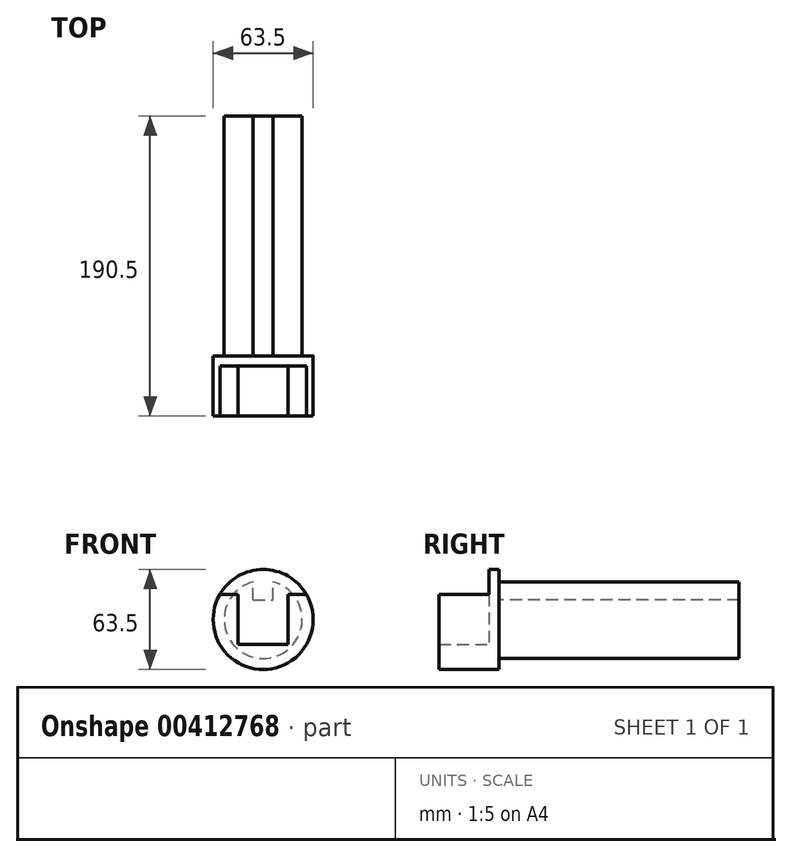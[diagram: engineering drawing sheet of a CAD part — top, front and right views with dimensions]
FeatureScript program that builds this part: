
annotation { "Feature Type Name" : "Feature", "Feature Type Description" : "" }
export const myFeature = defineFeature(function(context is Context, id is Id, definition is map)
    precondition{}
    {
        {
            var Q0;
            Q0=qCreatedBy(makeId("Front.planeOp"),FACE);
            var sketch = newSketch(context, id + "F0", { "sketchPlane" : qUnion([Q0])});
            skArc(sketch, "E0", {"start": v(-27.5, 15.88) * mm, "mid": v(0, -31.75) * mm, "end": v(27.5, 15.88) * mm});
            skLineSegment(sketch, "E1", {"start": v(0, 31.75) * mm, "end": v(0, -31.75) * mm, "construction": true});
            skCircle(sketch, "E2", {"center": v(0, 0) * mm, "radius": 22.45 * mm, "construction": true});
            skLineSegment(sketch, "E3", {"start": v(15.88, 15.88) * mm, "end": v(15.88, -15.88) * mm});
            skLineSegment(sketch, "E4", {"start": v(15.88, -15.88) * mm, "end": v(-15.88, -15.88) * mm});
            skLineSegment(sketch, "E5", {"start": v(-15.88, -15.88) * mm, "end": v(-15.88, 15.88) * mm});
            skLineSegment(sketch, "E6", {"start": v(-15.88, 15.88) * mm, "end": v(-27.5, 15.88) * mm});
            skLineSegment(sketch, "E7", {"start": v(15.88, 15.88) * mm, "end": v(27.5, 15.88) * mm});
            skArc(sketch, "E8", {"start": v(27.5, 15.88) * mm, "mid": v(0, 31.75) * mm, "end": v(-27.5, 15.88) * mm, "construction": true});
            skSolve(sketch);
        }
        {
            var Q0;
            Q0 = qSketchRegion(id + "F0", true);
            extrude(context, id + "F1", {"entities" : qUnion([Q0]), "depth" : 31.75 * mm, "offsetDistance" : 25.4 * mm});
        }
        {
            var Q0;
            Q0=makeQuery(id+"F1.opExtrude","CAP_FACE",FACE,{"disambiguationData":[OSD([sQuery(id+"F0.wireOp",EDGE,"E0"),sQuery(id+"F0.wireOp",EDGE,"ajWhx2Qm-t9gX-1MT6-eZGp-NJe44J70kVmW"),sQuery(id+"F0.wireOp",EDGE,"EVLei9R9-L3Dl-Atgz-0da7-zGIhw3F7YpG8"),sQuery(id+"F0.wireOp",EDGE,"9e28c039-71dc-46a3-9899-5aecf2effe9a0.MirrorCS"),sQuery(id+"F0.wireOp",EDGE,"9e28c039-71dc-46a3-9899-5aecf2effe9a1.MirrorCS")])],"isStart":true});
            var sketch = newSketch(context, id + "F2", { "sketchPlane" : qUnion([Q0])});
            skCircle(sketch, "E9", {"center": v(0, 0) * mm, "radius": 31.75 * mm});
            skSolve(sketch);
        }
        {
            var Q0;
            Q0 = qSketchRegion(id + "F2", true);
            extrude(context, id + "F3", {"entities" : qUnion([Q0]), "operationType" : NewBodyOperationType.ADD, "depth" : 6.35 * mm, "offsetDistance" : 25.4 * mm});
        }
        {
            var Q0;
            Q0=makeQuery(id+"F3.opExtrude","CAP_FACE",FACE,{"disambiguationData":[OSD([sQuery(id+"F2.wireOp",EDGE,"E9")])],"isStart":false});
            var sketch = newSketch(context, id + "F4", { "sketchPlane" : qUnion([Q0])});
            skArc(sketch, "E10.converted", {"start": v(-6.35, 23.94) * mm, "mid": v(0, -24.77) * mm, "end": v(6.35, 23.94) * mm});
            skLineSegment(sketch, "E11", {"start": v(0, 0) * mm, "end": v(0, 24.77) * mm, "construction": true});
            skLineSegment(sketch, "E12", {"start": v(0, 12.38) * mm, "end": v(-6.35, 12.38) * mm});
            skPoint(sketch, "E12.endSnap0", {"position": v(0, 12.38) * mm});
            skLineSegment(sketch, "E13", {"start": v(-6.35, 12.38) * mm, "end": v(-6.35, 23.94) * mm});
            skLineSegment(sketch, "E14.MirrorCS", {"start": v(6.35, 12.38) * mm, "end": v(6.35, 23.94) * mm});
            skLineSegment(sketch, "E15.MirrorCS", {"start": v(0, 12.38) * mm, "end": v(6.35, 12.38) * mm});
            skSolve(sketch);
        }
        {
            var Q0;
            Q0=makeQuery(id+"F4.imprint","IMPRINT",FACE,{"disambiguationData":[TD([[makeQuery(id+"F4.imprint","IMPRINT",EDGE,{"derivedFrom":sQuery(id+"F4.wireOp",EDGE,"E10.converted")}),1.0]])]});
            extrude(context, id + "F5", {"entities" : qUnion([Q0]), "operationType" : NewBodyOperationType.ADD, "depth" : 152.4 * mm, "offsetDistance" : 25.4 * mm});
        }
    });
